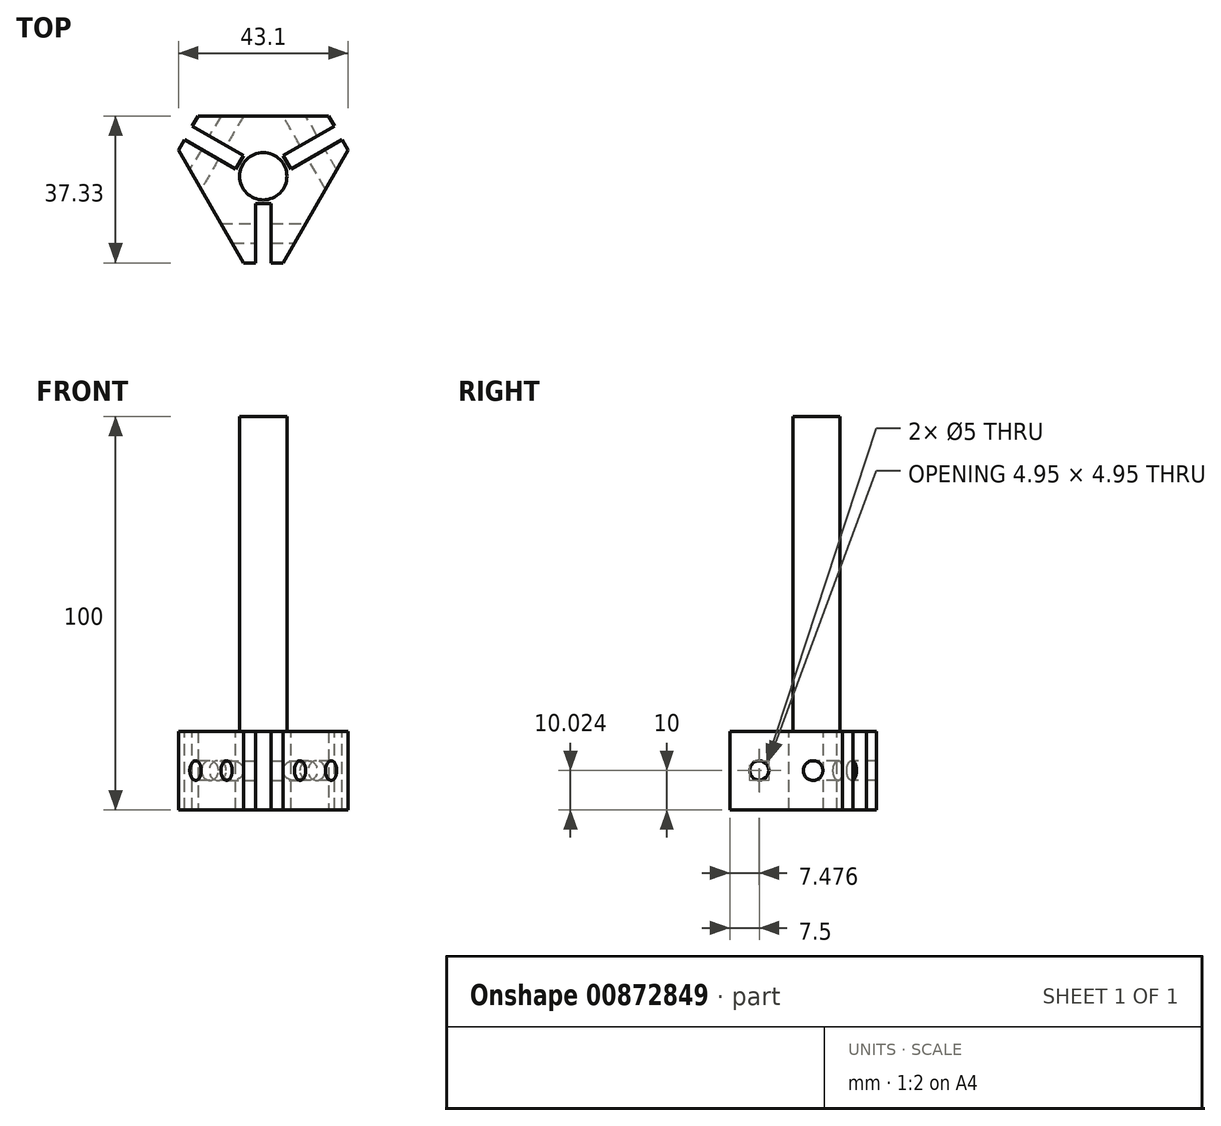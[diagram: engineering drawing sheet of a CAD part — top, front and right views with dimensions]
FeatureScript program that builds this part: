
annotation { "Feature Type Name" : "Feature", "Feature Type Description" : "" }
export const myFeature = defineFeature(function(context is Context, id is Id, definition is map)
    precondition{}
    {
        {
            var Q0;
            Q0=qCreatedBy(makeId("Top.planeOp"),FACE);
            var sketch = newSketch(context, id + "F0", { "sketchPlane" : qUnion([Q0])});
            skCircle(sketch, "E0.cCircle", {"center": v(0, 0) * mm, "radius": 15.33 * mm, "construction": true});
            skLineSegment(sketch, "E0.0", {"start": v(-16.55, 15.33) * mm, "end": v(16.55, 15.33) * mm});
            skLineSegment(sketch, "E0.1", {"start": v(21.55, 6.67) * mm, "end": v(5, -22) * mm});
            skLineSegment(sketch, "E0.2", {"start": v(-5, -22) * mm, "end": v(-21.55, 6.67) * mm});
            skPoint(sketch, "E0.0.midPoint", {"position": v(0, 15.33) * mm});
            skLineSegment(sketch, "E1", {"start": v(-16.55, 15.33) * mm, "end": v(-21.55, 6.67) * mm});
            skLineSegment(sketch, "E2", {"start": v(-5, -22) * mm, "end": v(5, -22) * mm});
            skLineSegment(sketch, "E3", {"start": v(16.55, 15.33) * mm, "end": v(21.55, 6.67) * mm});
            skPoint(sketch, "E4.orphan", {"position": v(26.55, 15.33) * mm});
            skPoint(sketch, "E5.orphan", {"position": v(0, -30.66) * mm});
            skPoint(sketch, "E6.orphan", {"position": v(-26.55, 15.33) * mm});
            skSolve(sketch);
        }
        {
            var Q0;
            Q0 = qSketchRegion(id + "F0", true);
            extrude(context, id + "F1", {"entities" : qUnion([Q0]), "depth" : 20 * mm, "offsetDistance" : 25 * mm});
        }
        {
            var Q0;
            Q0=makeQuery(id+"F1.opExtrude","CAP_FACE",FACE,{"disambiguationData":[OSD([sQuery(id+"F0.wireOp",EDGE,"E0.0"),sQuery(id+"F0.wireOp",EDGE,"E0.1"),sQuery(id+"F0.wireOp",EDGE,"E0.2"),sQuery(id+"F0.wireOp",EDGE,"E1"),sQuery(id+"F0.wireOp",EDGE,"E2"),sQuery(id+"F0.wireOp",EDGE,"E3")])],"isStart":false});
            var sketch = newSketch(context, id + "F2", { "sketchPlane" : qUnion([Q0])});
            skLineSegment(sketch, "E7.bottom", {"start": v(-2, -7) * mm, "end": v(2, -7) * mm});
            skLineSegment(sketch, "E7.top", {"start": v(-2, -22) * mm, "end": v(2, -22) * mm});
            skLineSegment(sketch, "E7.left", {"start": v(-2, -7) * mm, "end": v(-2, -22) * mm});
            skLineSegment(sketch, "E7.right", {"start": v(2, -7) * mm, "end": v(2, -22) * mm});
            skLineSegment(sketch, "E8", {"start": v(18.05, 12.73) * mm, "end": v(5.06, 5.23) * mm});
            skLineSegment(sketch, "E9", {"start": v(5.06, 5.23) * mm, "end": v(7.06, 1.77) * mm});
            skLineSegment(sketch, "E10", {"start": v(7.06, 1.77) * mm, "end": v(20.05, 9.27) * mm});
            skLineSegment(sketch, "E11", {"start": v(20.05, 9.27) * mm, "end": v(18.05, 12.73) * mm});
            skLineSegment(sketch, "E12", {"start": v(-18.05, 12.73) * mm, "end": v(-5.06, 5.23) * mm});
            skLineSegment(sketch, "E13", {"start": v(-5.06, 5.23) * mm, "end": v(-7.06, 1.77) * mm});
            skLineSegment(sketch, "E14", {"start": v(-18.05, 12.73) * mm, "end": v(-20.05, 9.27) * mm});
            skLineSegment(sketch, "E15", {"start": v(-20.05, 9.27) * mm, "end": v(-7.06, 1.77) * mm});
            skSolve(sketch);
        }
        {
            var Q0;
            Q0 = qSketchRegion(id + "F2", true);
            extrude(context, id + "F3", {"entities" : qUnion([Q0]), "operationType" : NewBodyOperationType.REMOVE, "oppositeDirection" : true, "depth" : 25 * mm, "offsetDistance" : 25 * mm});
        }
        {
            var Q0;
            Q0=makeQuery(id+"F1.opExtrude","CAP_FACE",FACE,{"disambiguationData":[OSD([sQuery(id+"F0.wireOp",EDGE,"E0.0"),sQuery(id+"F0.wireOp",EDGE,"E0.1"),sQuery(id+"F0.wireOp",EDGE,"E0.2"),sQuery(id+"F0.wireOp",EDGE,"E1"),sQuery(id+"F0.wireOp",EDGE,"E2"),sQuery(id+"F0.wireOp",EDGE,"E3")])],"isStart":false});
            var sketch = newSketch(context, id + "F4", { "sketchPlane" : qUnion([Q0])});
            skCircle(sketch, "E16", {"center": v(0, 0) * mm, "radius": 6 * mm});
            skSolve(sketch);
        }
        {
            var Q0;
            Q0 = qSketchRegion(id + "F4", true);
            extrude(context, id + "F5", {"entities" : qUnion([Q0]), "operationType" : NewBodyOperationType.ADD, "depth" : 80 * mm, "offsetDistance" : 25 * mm});
        }
        {
            var Q0;
            Q0=qCreatedBy(makeId("Right.planeOp"),FACE);
            var sketch = newSketch(context, id + "F6", { "sketchPlane" : qUnion([Q0])});
            skCircle(sketch, "E17", {"center": v(-14.5, 10) * mm, "radius": 2.5 * mm});
            skSolve(sketch);
        }
        {
            var Q0;
            Q0 = qSketchRegion(id + "F6", true);
            extrude(context, id + "F7", {"entities" : qUnion([Q0]), "operationType" : NewBodyOperationType.REMOVE, "endBound" : BoundingType.SYMMETRIC, "oppositeDirection" : true, "depth" : 25 * mm, "offsetDistance" : 25 * mm});
        }
        {
            var Q0;
            Q0=makeQuery(id+"F3.boolean.opBoolean","COPY",FACE,{"derivedFrom":makeQuery(id+"F3.opExtrude","SWEPT_FACE",FACE,{"disambiguationData":[OSD([sQuery(id+"F2.wireOp",EDGE,"E12")])]})});
            var sketch = newSketch(context, id + "F8", { "sketchPlane" : qUnion([Q0])});
            skCircle(sketch, "E18", {"center": v(-14.5, 10) * mm, "radius": 2.5 * mm});
            skSolve(sketch);
        }
        {
            var Q0;
            Q0 = qSketchRegion(id + "F8", true);
            extrude(context, id + "F9", {"entities" : qUnion([Q0]), "operationType" : NewBodyOperationType.REMOVE, "endBound" : BoundingType.SYMMETRIC, "oppositeDirection" : true, "depth" : 30 * mm, "offsetDistance" : 25 * mm});
        }
        {
            var Q0;
            Q0=makeQuery(id+"F3.boolean.opBoolean","COPY",FACE,{"derivedFrom":makeQuery(id+"F3.opExtrude","SWEPT_FACE",FACE,{"disambiguationData":[OSD([sQuery(id+"F2.wireOp",EDGE,"E10")])]})});
            var sketch = newSketch(context, id + "F10", { "sketchPlane" : qUnion([Q0])});
            skCircle(sketch, "E19", {"center": v(-14.5, 10) * mm, "radius": 2.5 * mm});
            skSolve(sketch);
        }
        {
            var Q0;
            Q0 = qSketchRegion(id + "F10", true);
            extrude(context, id + "F11", {"entities" : qUnion([Q0]), "operationType" : NewBodyOperationType.REMOVE, "endBound" : BoundingType.SYMMETRIC, "oppositeDirection" : true, "depth" : 30 * mm, "offsetDistance" : 25 * mm});
        }
    });
